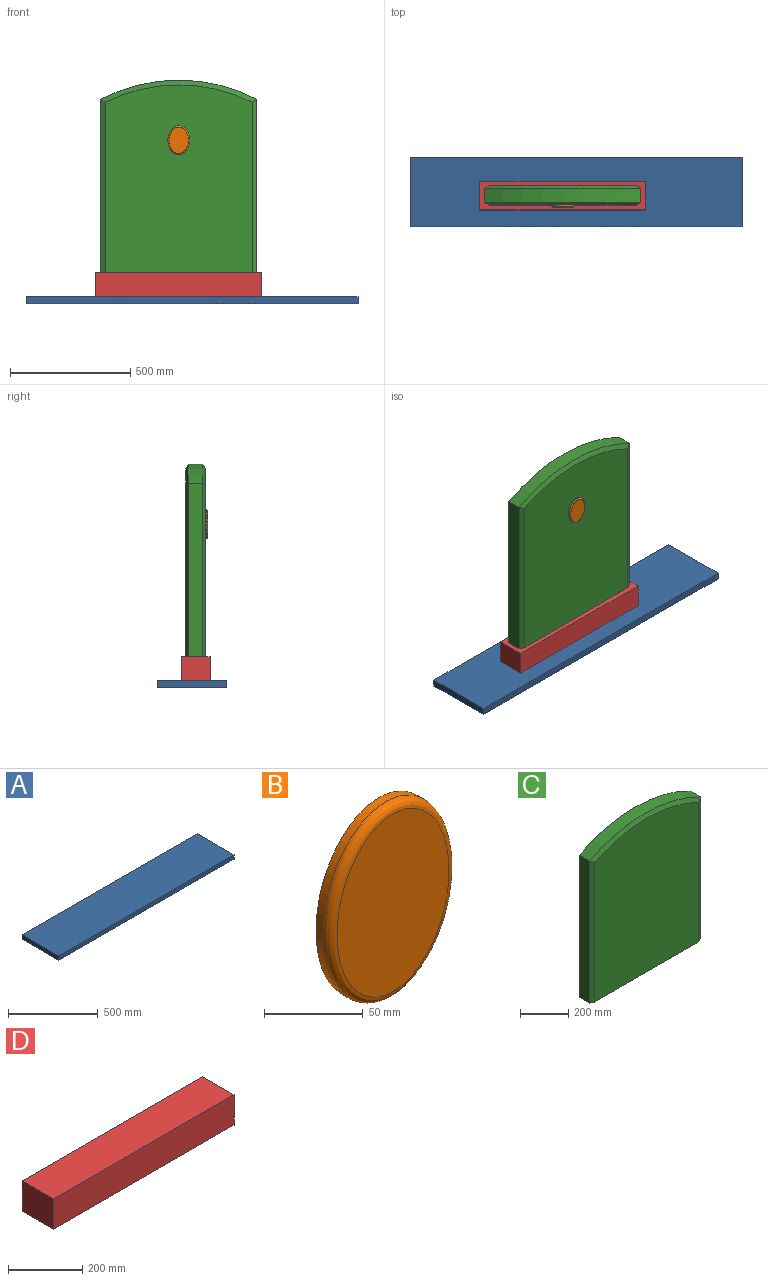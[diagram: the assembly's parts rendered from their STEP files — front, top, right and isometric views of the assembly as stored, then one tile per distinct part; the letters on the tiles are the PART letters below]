
ASSEMBLY  parts=4 mates=2
PART A: 6 faces, bbox 1380x290x30 mm
  f0: plane 290x30mm, normal (-1,0,0), area 8700mm2, adj f1,f3,f4,f5
  f1: plane 1380x30mm, normal (0,-1,0), area 41400mm2, adj f0,f2,f4,f5
  f2: plane 290x30mm, normal (1,0,0), area 8700mm2, adj f1,f3,f4,f5
  f3: plane 1380x30mm, normal (0,1,0), area 41400mm2, adj f0,f2,f4,f5
  f4: plane 1380x290mm, normal (0,0,1), area 400200mm2, adj f0,f1,f2,f3
  f5: plane 1380x290mm, normal (0,0,-1), area 400200mm2, adj f0,f1,f2,f3
PART B: 4 faces, bbox 90x10x120 mm
  f0: extruded ~120x90mm, area 1657.8mm2, adj f2,f3
  f1: plane 110.01x80.02mm, normal (0,-1,0), area 6900mm2, adj f3
  f2: plane 120x90mm, normal (0,1,0), area 8482.3mm2, adj f0
  f3: bspline ~120.02x90.03mm, area 2513.9mm2, adj f0,f1
PART C: 12 faces, bbox 650x80x800 mm
  f0: cylinder r=700mm len=650mm, axis (0,1,0), area 40557.5mm2, adj f1,f3,f6,f9
  f1: plane 719.98x60mm, normal (-1,0,0), area 43198.8mm2, adj f0,f2,f7,f8
  f2: plane 650x80mm, normal (0,0,-1), area 51600mm2, adj f1,f3,f4,f5,f7,f8,f10,f11
  f3: plane 719.98x60mm, normal (1,0,0), area 43198.8mm2, adj f0,f2,f10,f11
  f4: plane 780x610mm, normal (0,-1,0), area 461438.7mm2, adj f2,f8,f9,f10
  f5: plane 780x610mm, normal (0,1,0), area 461438.7mm2, adj f2,f6,f7,f11
  f6: cone r=700mm half-angle=63.4deg, axis (0,-1,0), area 14629.3mm2, adj f0,f5,f7,f11
  f7: plane 719.98x20mm, normal (-0.45,0.89,0), area 15963.1mm2, adj f1,f2,f5,f6
  f8: plane 719.98x20mm, normal (-0.45,-0.89,0), area 15963.1mm2, adj f1,f2,f4,f9
  f9: cone r=680mm half-angle=63.4deg, axis (0,1,0), area 14629.3mm2, adj f0,f4,f8,f10
  f10: plane 719.98x20mm, normal (0.45,-0.89,0), area 15963.1mm2, adj f2,f3,f4,f9
  f11: plane 719.98x20mm, normal (0.45,0.89,0), area 15963.1mm2, adj f2,f3,f5,f6
PART D: 6 faces, bbox 690x120x100 mm
  f0: plane 690x120mm, normal (0,0,1), area 82800mm2, adj f1,f3,f4,f5
  f1: plane 120x100mm, normal (-1,0,0), area 12000mm2, adj f0,f2,f4,f5
  f2: plane 690x120mm, normal (0,0,-1), area 82800mm2, adj f1,f3,f4,f5
  f3: plane 120x100mm, normal (1,0,0), area 12000mm2, adj f0,f2,f4,f5
  f4: plane 690x100mm, normal (0,-1,0), area 69000mm2, adj f0,f1,f2,f3
  f5: plane 690x100mm, normal (0,1,0), area 69000mm2, adj f0,f1,f2,f3
PLACE A at identity
PLACE B t=(635,1370,-50)mm
PLACE C t=(635,1370,0)mm
PLACE D t=(635,1370,0)mm
MATE fastened D.f0 <-> C.f2  axis (0,0,1) through (635,1370,130)mm
MATE fastened B.f2 <-> C.f4  axis (0,1,0) through (635,1330,680)mm
